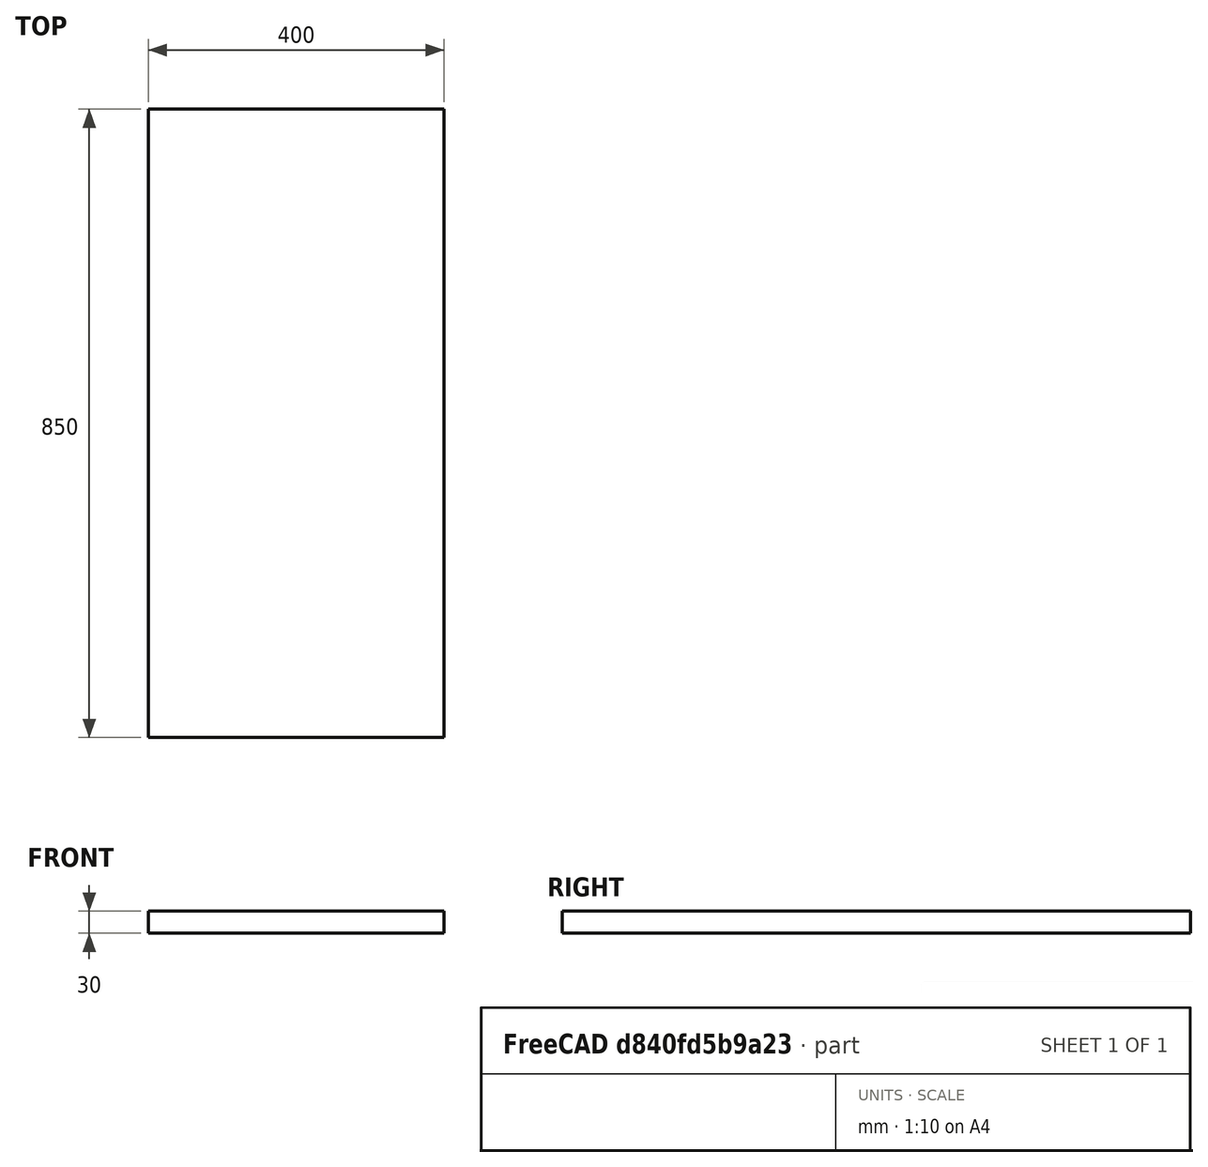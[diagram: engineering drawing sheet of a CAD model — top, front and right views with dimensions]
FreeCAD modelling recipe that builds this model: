
FCSTD DOCUMENT  (FreeCAD 1.0R39319 (Git))
Label: base-plate-big
License: All rights reserved
LicenseURL: https://en.wikipedia.org/wiki/All_rights_reserved
objects: Sketcher::SketchObject×1, PartDesign::Pad×1, PartDesign::Body×1
note: 6 computed .brp shape members not serialized (recipe doc carries the construction recipe); baked Part::Feature solids carry a one-line shape summary decoded from their .brp

FEATURE [Sketcher::SketchObject] Sketch
  ArcFitTolerance = 1e-06
  AttachmentSupport = -> [XY_Plane]
  FullyConstrained = true
  MakeInternals = false
  MapMode = 5
  sketch-geometry (4):
    g0: LineSegment StartX=0 StartY=0 StartZ=0 EndX=400 EndY=0 EndZ=0
    g1: LineSegment StartX=400 StartY=0 StartZ=0 EndX=400 EndY=850 EndZ=0
    g2: LineSegment StartX=400 StartY=850 StartZ=0 EndX=0 EndY=850 EndZ=0
    g3: LineSegment StartX=0 StartY=850 StartZ=0 EndX=0 EndY=0 EndZ=0
  constraints (11):
    c: Coincident(g0,g1)
    c: Coincident(g1,g2)
    c: Coincident(g2,g3)
    c: Coincident(g3,g0)
    c: Horizontal(g0)
    c: Horizontal(g2)
    c: Vertical(g1)
    c: Vertical(g3)
    c: Distance(g1,g3) = 400
    c: Distance(g0,g2) = 850
    c: Coincident(g0,g-1)
FEATURE [PartDesign::Pad] Pad
  Direction = (0,0,1)
  Length = 30
  Length2 = 10
  Profile = -> Sketch
  ReferenceAxis = -> Sketch [N_Axis]
  Refine = true
  Suppressed = false
  Type = 0
FEATURE [PartDesign::Body] Body
  AllowCompound = false
  Group = -> [Sketch,Pad]
  Origin = -> Origin
  Tip = -> Pad
